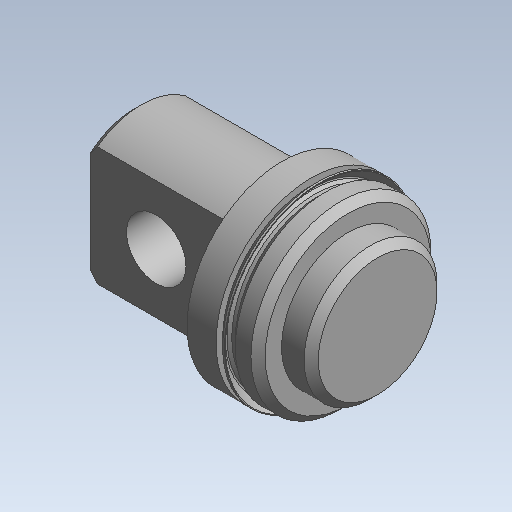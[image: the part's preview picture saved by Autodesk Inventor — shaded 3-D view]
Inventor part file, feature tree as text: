
AUTODESK INVENTOR PART (.ipt)
format: ipt  version: 2020 (Build 240168000, 168)  size: 239,104 bytes
history: native  units: mm (DEFAULTED — no unit token found)
features: other x140, sketch x6, revolve x4, extrude x2
ambient origin geometry x8: Origin, YZ Plane, XZ Plane, XY Plane, X Axis, Y Axis, Z Axis, Center Point
bodies: Solid1 (feature_tree)
feature tree (152):
  revolve  "Revolution1"  Angle=360.0deg
  revolve  "Revolution2"  Angle=360.0deg
  revolve  "Revolution3"  [1 undecoded]
  revolve  "Revolution4"  [1 undecoded]
  extrude  "Extrusion1"  [1 undecoded]
  extrude  "Extrusion2"  [1 undecoded]
  other  "1_XY"
  other  "1_YZ"
  other  "1_ZX"
  other  "1_X"
  other  "1_Y"
  other  "1_Z"
  other  "1_Center"
  other  "lovra_XY"
  other  "lovra_YZ"
  other  "lovra_ZX"
  other  "lovra_X"
  other  "lovra_Y"
  other  "lovra_Z"
  other  "lovra_Center"
  other  "lovra1_XY"
  other  "lovra1_YZ"
  other  "lovra1_ZX"
  other  "lovra1_X"
  other  "lovra1_Y"
  other  "lovra1_Z"
  other  "lovra1_Center"
  other  "lovra2_XY"
  other  "lovra2_YZ"
  other  "lovra2_ZX"
  other  "lovra2_X"
  other  "lovra2_Y"
  other  "lovra2_Z"
  other  "lovra2_Center"
  other  "lovra21_XY"
  other  "lovra21_YZ"
  other  "lovra21_ZX"
  other  "lovra21_X"
  other  "lovra21_Y"
  other  "lovra21_Z"
  other  "lovra21_Center"
  other  "lovra22_XY"
  other  "lovra22_YZ"
  other  "lovra22_ZX"
  other  "lovra22_X"
  other  "lovra22_Y"
  other  "lovra22_Z"
  other  "lovra22_Center"
  other  "lovra3_XY"
  other  "lovra3_YZ"
  other  "lovra3_ZX"
  other  "lovra3_X"
  other  "lovra3_Y"
  other  "lovra3_Z"
  other  "lovra3_Center"
  other  "olen_XY"
  other  "olen_YZ"
  other  "olen_ZX"
  other  "olen_X"
  other  "olen_Y"
  other  "olen_Z"
  other  "olen_Center"
  other  "p1_XY"
  other  "p1_YZ"
  other  "p1_ZX"
  other  "p1_X"
  other  "p1_Y"
  other  "p1_Z"
  other  "p1_Center"
  other  "p2_XY"
  other  "p2_YZ"
  other  "p2_ZX"
  other  "p2_X"
  other  "p2_Y"
  other  "p2_Z"
  other  "p2_Center"
  other  "port2_XY"
  other  "port2_YZ"
  other  "port2_ZX"
  other  "port2_X"
  other  "port2_Y"
  other  "port2_Z"
  other  "port2_Center"
  other  "thd1_XY"
  other  "thd1_YZ"
  other  "thd1_ZX"
  other  "thd1_X"
  other  "thd1_Y"
  other  "thd1_Z"
  other  "thd1_Center"
  other  "thd2_XY"
  other  "thd2_YZ"
  other  "thd2_ZX"
  other  "thd2_X"
  other  "thd2_Y"
  other  "thd2_Z"
  other  "thd2_Center"
  other  "to_mounting_bracket_XY"
  other  "to_mounting_bracket_YZ"
  other  "to_mounting_bracket_ZX"
  other  "to_mounting_bracket_X"
  other  "to_mounting_bracket_Y"
  other  "to_mounting_bracket_Z"
  other  "to_mounting_bracket_Center"
  other  "to_nut_XY"
  other  "to_nut_YZ"
  other  "to_nut_ZX"
  other  "to_nut_X"
  other  "to_nut_Y"
  other  "to_nut_Z"
  other  "to_nut_Center"
  other  "to_pin_XY"
  other  "to_pin_YZ"
  other  "to_pin_ZX"
  other  "to_pin_X"
  other  "to_pin_Y"
  other  "to_pin_Z"
  other  "to_pin_Center"
  other  "to_pin_1_XY"
  other  "to_pin_1_YZ"
  other  "to_pin_1_ZX"
  other  "to_pin_1_X"
  other  "to_pin_1_Y"
  other  "to_pin_1_Z"
  other  "to_pin_1_Center"
  other  "to_pin_r_XY"
  other  "to_pin_r_YZ"
  other  "to_pin_r_ZX"
  other  "to_pin_r_X"
  other  "to_pin_r_Y"
  other  "to_pin_r_Z"
  other  "to_pin_r_Center"
  other  "to_screw_XY"
  other  "to_screw_YZ"
  other  "to_screw_ZX"
  other  "to_screw_X"
  other  "to_screw_Y"
  other  "to_screw_Z"
  other  "to_screw_Center"
  other  "to_tube_XY"
  other  "to_tube_YZ"
  other  "to_tube_ZX"
  other  "to_tube_X"
  other  "to_tube_Y"
  other  "to_tube_Z"
  other  "to_tube_Center"
  sketch  "Sketch_1"  dims[d0=360.0deg d1=360.0deg]
  sketch  "Sketch_24"  dims[d2=360.0deg d3=360.0deg]
  sketch  "Sketch_26"  dims[d4=15.875mm d5=0.0mm d6=18.923mm d7=0.0mm]
  sketch  "Sketch_27"  dims[d8=0.0mm d9=0.0mm d10=0.0mm d11=0.0mm d12=0.0mm d13=0.0mm d14=0.0mm]
  sketch  "Sketch_28"
  sketch  "Sketch_29"
note: 4 required parameter values undecoded (feature->parameter linkage not recoverable at this tier; creation-order binding heuristic only, values carry confidence <= 0.55)